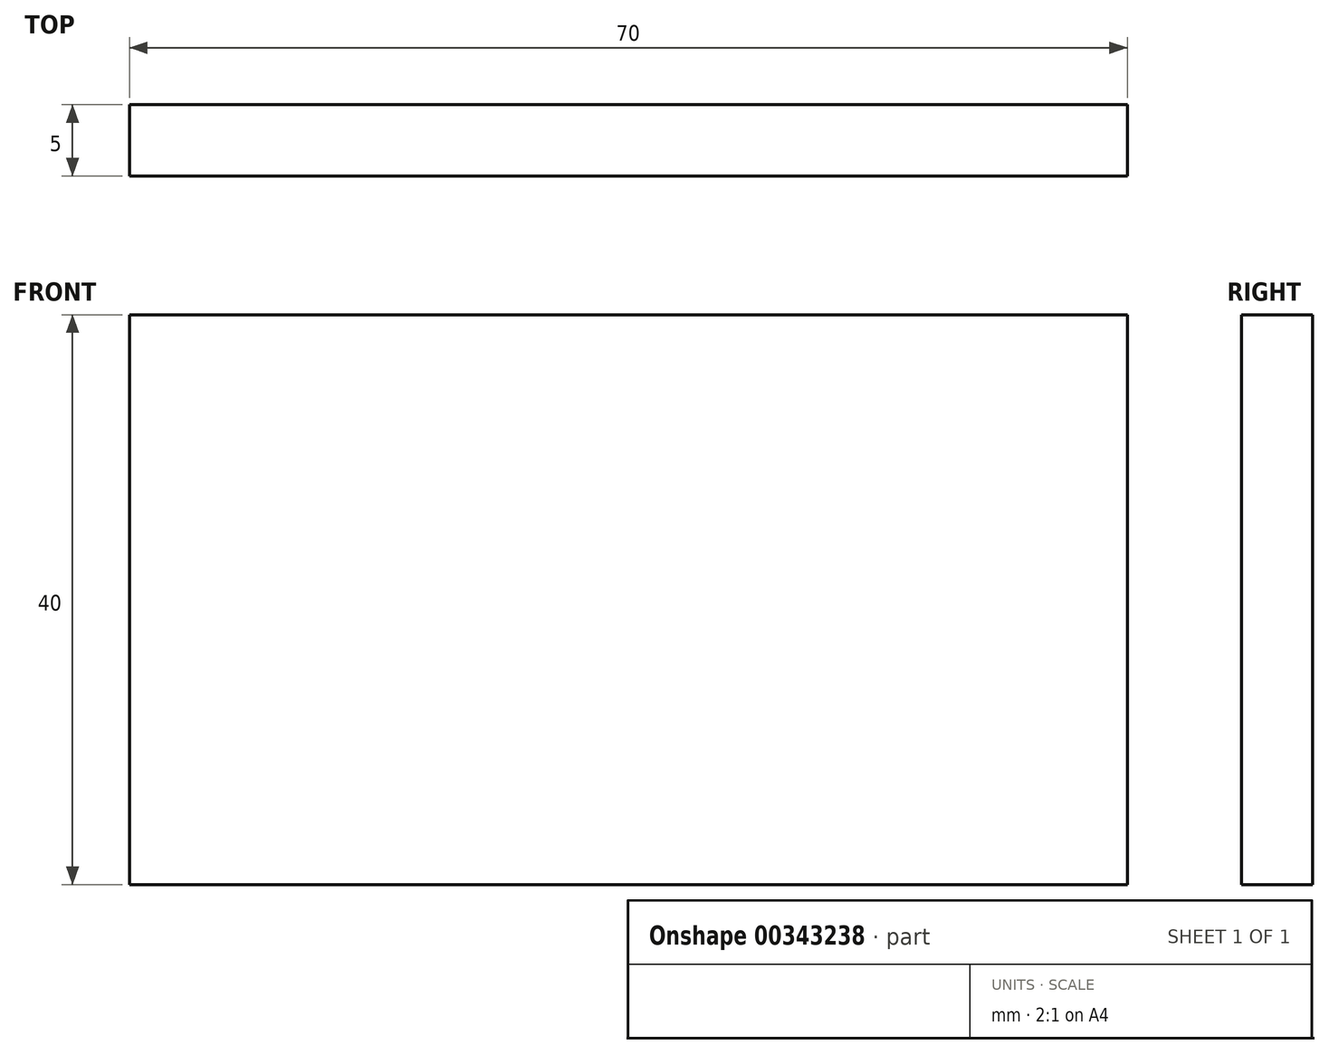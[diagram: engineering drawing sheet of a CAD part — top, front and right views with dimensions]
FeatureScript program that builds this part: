
annotation { "Feature Type Name" : "Feature", "Feature Type Description" : "" }
export const myFeature = defineFeature(function(context is Context, id is Id, definition is map)
    precondition{}
    {
        {
            var Q0;
            Q0=qCreatedBy(makeId("Front.planeOp"),FACE);
            var sketch = newSketch(context, id + "F0", { "sketchPlane" : qUnion([Q0])});
            skLineSegment(sketch, "E0.bottom", {"start": v(35, 20) * mm, "end": v(-35, 20) * mm});
            skLineSegment(sketch, "E0.top", {"start": v(35, -20) * mm, "end": v(-35, -20) * mm});
            skLineSegment(sketch, "E0.left", {"start": v(35, 20) * mm, "end": v(35, -20) * mm});
            skLineSegment(sketch, "E0.right", {"start": v(-35, 20) * mm, "end": v(-35, -20) * mm});
            skPoint(sketch, "E0.middle", {"position": v(0, 0) * mm});
            skSolve(sketch);
        }
        {
            var Q0;
            Q0=makeQuery(id+"F0.imprint","IMPRINT",FACE,{"disambiguationData":[TD([[makeQuery(id+"F0.imprint","IMPRINT",EDGE,{"derivedFrom":sQuery(id+"F0.wireOp",EDGE,"E0.bottom")}),1.0]])]});
            extrude(context, id + "F1", {"entities" : qUnion([Q0]), "depth" : 5 * mm});
        }
    });
